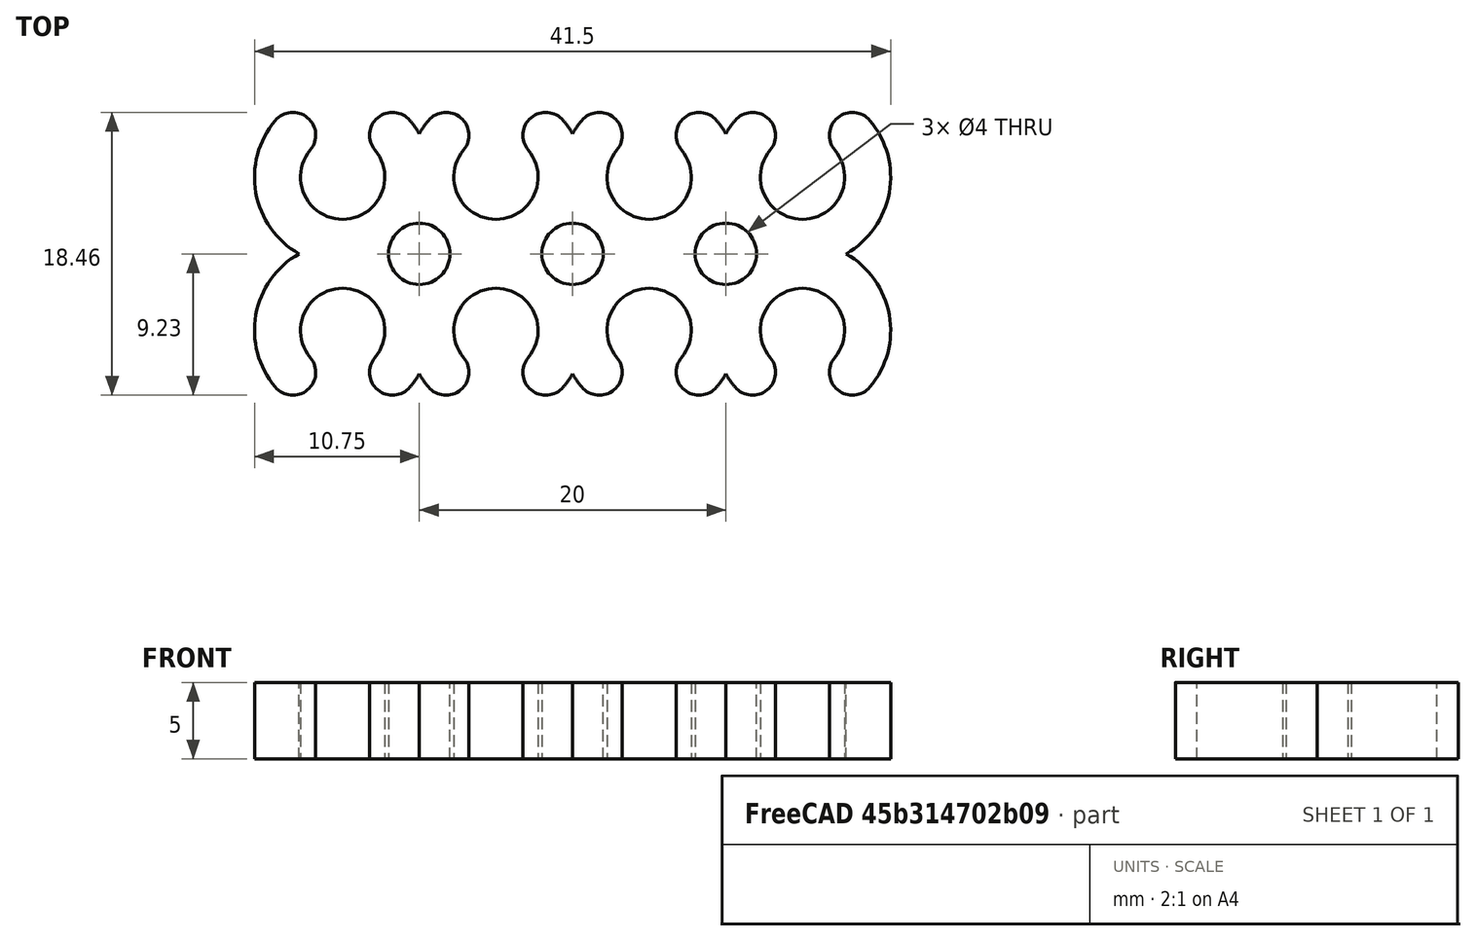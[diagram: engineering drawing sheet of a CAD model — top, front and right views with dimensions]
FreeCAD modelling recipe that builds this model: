
FCSTD DOCUMENT  (FreeCAD 0.19R24276 (Git))
Label: EthernetCableBondage
License: All rights reserved
LicenseURL: http://en.wikipedia.org/wiki/All_rights_reserved
objects: TechDraw::DrawViewDimension×4, Sketcher::SketchObject×1, PartDesign::Pad×1, PartDesign::Body×1, TechDraw::DrawSVGTemplate×1, TechDraw::DrawViewPart×1, Spreadsheet::Sheet×1, TechDraw::DrawViewAnnotation×1, TechDraw::DrawPage×1
note: 4 computed .brp shape members not serialized (recipe doc carries the construction recipe); baked Part::Feature solids carry a one-line shape summary decoded from their .brp

FEATURE [Sketcher::SketchObject] Sketch
  FullyConstrained = true
  MapMode = 5
  Support = -> [XY_Plane]
  expr: Constraints[18] = Spreadsheet.B2
  expr: Constraints[97] = Spreadsheet.B3
  expr: Constraints[194] = Spreadsheet.B3
  expr: Constraints[59] = Spreadsheet.B2
  expr: Constraints[116] = Spreadsheet.B2
  expr: Constraints[162] = Spreadsheet.B2
  expr: Constraints[106] = Spreadsheet.B2
  expr: Constraints[149] = Spreadsheet.B3
  expr: Constraints[51] = Spreadsheet.B3
  expr: Constraints[202] = Spreadsheet.B3
  expr: Constraints[52] = Spreadsheet.B3
  expr: Constraints[148] = Spreadsheet.B3
  expr: Constraints[101] = Spreadsheet.B3
  sketch-geometry (72):
    g0: LineSegment StartX=10 StartY=15 StartZ=0 EndX=40 EndY=15 EndZ=0
    g1: LineSegment StartX=10 StartY=20 StartZ=0 EndX=10 EndY=10 EndZ=0
    g2: LineSegment StartX=20 StartY=20 StartZ=0 EndX=20 EndY=10 EndZ=0
    g3: LineSegment StartX=30 StartY=20 StartZ=0 EndX=30 EndY=10 EndZ=0
    g4: LineSegment StartX=40 StartY=20 StartZ=0 EndX=40 EndY=10 EndZ=0
    g5: ArcOfCircle CenterX=10 CenterY=20 CenterZ=0 NormalX=0 NormalY=0 NormalZ=1 AngleXU=0 Radius=2.75 StartAngle=2.44346 EndAngle=6.98132
    g6: ArcOfCircle CenterX=10 CenterY=10 CenterZ=0 NormalX=0 NormalY=0 NormalZ=1 AngleXU=0 Radius=2.75 StartAngle=5.58505 EndAngle=10.1229
    g7: ArcOfCircle CenterX=10 CenterY=20 CenterZ=0 NormalX=0 NormalY=0 NormalZ=1 AngleXU=0 Radius=5.75 StartAngle=2.44346 EndAngle=4.19591
    g8: ArcOfCircle CenterX=10 CenterY=10 CenterZ=0 NormalX=0 NormalY=0 NormalZ=1 AngleXU=0 Radius=5.75 StartAngle=2.08727 EndAngle=3.83972
    g9: ArcOfCircle CenterX=10 CenterY=20 CenterZ=0 NormalX=0 NormalY=0 NormalZ=1 AngleXU=0 Radius=5.75 StartAngle=0.516475 EndAngle=0.698132
    g10: ArcOfCircle CenterX=10 CenterY=10 CenterZ=0 NormalX=0 NormalY=0 NormalZ=1 AngleXU=0 Radius=5.75 StartAngle=5.58505 EndAngle=5.76671
    g11: ArcOfCircle CenterX=6.74431 CenterY=22.7318 CenterZ=0 NormalX=0 NormalY=0 NormalZ=1 AngleXU=0 Radius=1.5 StartAngle=5.58505 EndAngle=8.72665
    g12: ArcOfCircle CenterX=13.2557 CenterY=22.7318 CenterZ=0 NormalX=0 NormalY=0 NormalZ=1 AngleXU=0 Radius=1.5 StartAngle=0.698132 EndAngle=3.83972
    g13: ArcOfCircle CenterX=6.74431 CenterY=7.26815 CenterZ=0 NormalX=0 NormalY=0 NormalZ=1 AngleXU=0 Radius=1.5 StartAngle=3.83972 EndAngle=6.98132
    g14: ArcOfCircle CenterX=13.2557 CenterY=7.26815 CenterZ=0 NormalX=0 NormalY=0 NormalZ=1 AngleXU=0 Radius=1.5 StartAngle=2.44346 EndAngle=5.58505
    g15: LineSegment StartX=10 StartY=20 StartZ=0 EndX=5.59524 EndY=23.696 EndZ=0
    g16: LineSegment StartX=10 StartY=20 StartZ=0 EndX=14.4048 EndY=23.696 EndZ=0
    g17: LineSegment StartX=10 StartY=10 StartZ=0 EndX=5.59524 EndY=6.30397 EndZ=0
    g18: LineSegment StartX=10 StartY=10 StartZ=0 EndX=14.4048 EndY=6.30397 EndZ=0
    g19: ArcOfCircle CenterX=20 CenterY=20 CenterZ=0 NormalX=0 NormalY=0 NormalZ=1 AngleXU=0 Radius=2.75 StartAngle=2.44346 EndAngle=6.98132
    g20: ArcOfCircle CenterX=20 CenterY=10 CenterZ=0 NormalX=0 NormalY=0 NormalZ=1 AngleXU=0 Radius=2.75 StartAngle=5.58505 EndAngle=10.1229
    g21: ArcOfCircle CenterX=20 CenterY=20 CenterZ=0 NormalX=0 NormalY=0 NormalZ=1 AngleXU=0 Radius=5.75 StartAngle=2.44346 EndAngle=2.62512
    g22: ArcOfCircle CenterX=16.7443 CenterY=22.7318 CenterZ=0 NormalX=0 NormalY=0 NormalZ=1 AngleXU=0 Radius=1.5 StartAngle=5.58505 EndAngle=8.72665
    g23: LineSegment StartX=20 StartY=20 StartZ=0 EndX=15.5952 EndY=23.696 EndZ=0
    g24: LineSegment StartX=7.89338 StartY=21.7677 StartZ=0 EndX=12.1066 EndY=21.7677 EndZ=0
    g25: LineSegment StartX=7.89338 StartY=8.23233 StartZ=0 EndX=12.1066 EndY=8.23233 EndZ=0
    g26: ArcOfCircle CenterX=20 CenterY=20 CenterZ=0 NormalX=0 NormalY=0 NormalZ=1 AngleXU=0 Radius=5.75 StartAngle=0.516475 EndAngle=0.698132
    g27: ArcOfCircle CenterX=20 CenterY=10 CenterZ=0 NormalX=0 NormalY=0 NormalZ=1 AngleXU=0 Radius=5.75 StartAngle=3.65807 EndAngle=3.83972
    g28: ArcOfCircle CenterX=20 CenterY=10 CenterZ=0 NormalX=0 NormalY=0 NormalZ=1 AngleXU=0 Radius=5.75 StartAngle=5.58505 EndAngle=5.76671
    g29: ArcOfCircle CenterX=16.7443 CenterY=7.26815 CenterZ=0 NormalX=0 NormalY=0 NormalZ=1 AngleXU=0 Radius=1.5 StartAngle=3.83972 EndAngle=6.98132
    g30: ArcOfCircle CenterX=23.2557 CenterY=7.26815 CenterZ=0 NormalX=0 NormalY=0 NormalZ=1 AngleXU=0 Radius=1.5 StartAngle=2.44346 EndAngle=5.58505
    g31: ArcOfCircle CenterX=23.2557 CenterY=22.7318 CenterZ=0 NormalX=0 NormalY=0 NormalZ=1 AngleXU=0 Radius=1.5 StartAngle=0.698132 EndAngle=3.83972
    g32: LineSegment StartX=20 StartY=20 StartZ=0 EndX=24.4048 EndY=23.696 EndZ=0
    g33: LineSegment StartX=20 StartY=10 StartZ=0 EndX=15.5952 EndY=6.30397 EndZ=0
    g34: LineSegment StartX=20 StartY=10 StartZ=0 EndX=24.4048 EndY=6.30397 EndZ=0
    g35: LineSegment StartX=17.8934 StartY=21.7677 StartZ=0 EndX=22.1066 EndY=21.7677 EndZ=0
    g36: LineSegment StartX=17.8934 StartY=8.23233 StartZ=0 EndX=22.1066 EndY=8.23233 EndZ=0
    g37: Circle CenterX=15 CenterY=15 CenterZ=0 NormalX=0 NormalY=0 NormalZ=1 AngleXU=0 Radius=2
    g38: ArcOfCircle CenterX=30 CenterY=20 CenterZ=0 NormalX=0 NormalY=0 NormalZ=1 AngleXU=0 Radius=2.75 StartAngle=2.44346 EndAngle=6.98132
    g39: ArcOfCircle CenterX=30 CenterY=20 CenterZ=0 NormalX=0 NormalY=0 NormalZ=1 AngleXU=0 Radius=5.75 StartAngle=2.44346 EndAngle=2.62512
    g40: ArcOfCircle CenterX=30 CenterY=20 CenterZ=0 NormalX=0 NormalY=0 NormalZ=1 AngleXU=0 Radius=5.75 StartAngle=0.516475 EndAngle=0.698132
    g41: ArcOfCircle CenterX=30 CenterY=10 CenterZ=0 NormalX=0 NormalY=0 NormalZ=1 AngleXU=0 Radius=2.75 StartAngle=5.58505 EndAngle=10.1229
    g42: ArcOfCircle CenterX=30 CenterY=10 CenterZ=0 NormalX=0 NormalY=0 NormalZ=1 AngleXU=0 Radius=5.75 StartAngle=3.65807 EndAngle=3.83972
    g43: ArcOfCircle CenterX=30 CenterY=10 CenterZ=0 NormalX=0 NormalY=0 NormalZ=1 AngleXU=0 Radius=5.75 StartAngle=5.58505 EndAngle=5.76671
    g44: ArcOfCircle CenterX=26.7443 CenterY=22.7318 CenterZ=0 NormalX=0 NormalY=0 NormalZ=1 AngleXU=0 Radius=1.5 StartAngle=5.58505 EndAngle=8.72665
    g45: ArcOfCircle CenterX=26.7443 CenterY=7.26815 CenterZ=0 NormalX=0 NormalY=0 NormalZ=1 AngleXU=0 Radius=1.5 StartAngle=3.83972 EndAngle=6.98132
    g46: ArcOfCircle CenterX=33.2557 CenterY=22.7318 CenterZ=0 NormalX=0 NormalY=0 NormalZ=1 AngleXU=0 Radius=1.5 StartAngle=0.698132 EndAngle=3.83972
    g47: ArcOfCircle CenterX=33.2557 CenterY=7.26815 CenterZ=0 NormalX=0 NormalY=0 NormalZ=1 AngleXU=0 Radius=1.5 StartAngle=2.44346 EndAngle=5.58505
    g48: LineSegment StartX=30 StartY=20 StartZ=0 EndX=25.5952 EndY=23.696 EndZ=0
    g49: LineSegment StartX=30 StartY=20 StartZ=0 EndX=34.4048 EndY=23.696 EndZ=0
    g50: LineSegment StartX=30 StartY=10 StartZ=0 EndX=25.5952 EndY=6.30397 EndZ=0
    g51: LineSegment StartX=30 StartY=10 StartZ=0 EndX=34.4048 EndY=6.30397 EndZ=0
    g52: LineSegment StartX=27.8934 StartY=21.7677 StartZ=0 EndX=32.1066 EndY=21.7677 EndZ=0
    g53: LineSegment StartX=27.8934 StartY=8.23233 StartZ=0 EndX=32.1066 EndY=8.23233 EndZ=0
    g54: ArcOfCircle CenterX=40 CenterY=20 CenterZ=0 NormalX=0 NormalY=0 NormalZ=1 AngleXU=0 Radius=2.75 StartAngle=2.44346 EndAngle=6.98132
    g55: ArcOfCircle CenterX=40 CenterY=20 CenterZ=0 NormalX=0 NormalY=0 NormalZ=1 AngleXU=0 Radius=5.75 StartAngle=2.44346 EndAngle=2.62512
    g56: ArcOfCircle CenterX=40 CenterY=20 CenterZ=0 NormalX=0 NormalY=0 NormalZ=1 AngleXU=0 Radius=5.75 StartAngle=5.22886 EndAngle=6.98132
    g57: ArcOfCircle CenterX=40 CenterY=10 CenterZ=0 NormalX=0 NormalY=0 NormalZ=1 AngleXU=0 Radius=2.75 StartAngle=5.58505 EndAngle=10.1229
    g58: ArcOfCircle CenterX=40 CenterY=10 CenterZ=0 NormalX=0 NormalY=0 NormalZ=1 AngleXU=0 Radius=5.75 StartAngle=3.65807 EndAngle=3.83972
    g59: ArcOfCircle CenterX=40 CenterY=10 CenterZ=0 NormalX=0 NormalY=0 NormalZ=1 AngleXU=0 Radius=5.75 StartAngle=5.58505 EndAngle=7.33751
    g60: ArcOfCircle CenterX=36.7443 CenterY=22.7318 CenterZ=0 NormalX=0 NormalY=0 NormalZ=1 AngleXU=0 Radius=1.5 StartAngle=5.58505 EndAngle=8.72665
    g61: ArcOfCircle CenterX=43.2557 CenterY=22.7318 CenterZ=0 NormalX=0 NormalY=0 NormalZ=1 AngleXU=0 Radius=1.5 StartAngle=0.698132 EndAngle=3.83972
    g62: ArcOfCircle CenterX=36.7443 CenterY=7.26815 CenterZ=0 NormalX=0 NormalY=0 NormalZ=1 AngleXU=0 Radius=1.5 StartAngle=3.83972 EndAngle=6.98132
    g63: ArcOfCircle CenterX=43.2557 CenterY=7.26815 CenterZ=0 NormalX=0 NormalY=0 NormalZ=1 AngleXU=0 Radius=1.5 StartAngle=2.44346 EndAngle=5.58505
    g64: LineSegment StartX=40 StartY=20 StartZ=0 EndX=35.5952 EndY=23.696 EndZ=0
    g65: LineSegment StartX=40 StartY=20 StartZ=0 EndX=44.4048 EndY=23.696 EndZ=0
    g66: LineSegment StartX=40 StartY=10 StartZ=0 EndX=35.5952 EndY=6.30397 EndZ=0
    g67: LineSegment StartX=40 StartY=10 StartZ=0 EndX=44.4048 EndY=6.30397 EndZ=0
    g68: LineSegment StartX=37.8934 StartY=21.7677 StartZ=0 EndX=42.1066 EndY=21.7677 EndZ=0
    g69: LineSegment StartX=37.8934 StartY=8.23233 StartZ=0 EndX=42.1066 EndY=8.23233 EndZ=0
    g70: Circle CenterX=25 CenterY=15 CenterZ=0 NormalX=0 NormalY=0 NormalZ=1 AngleXU=0 Radius=2
    g71: Circle CenterX=35 CenterY=15 CenterZ=0 NormalX=0 NormalY=0 NormalZ=1 AngleXU=0 Radius=2
  constraints (209):
    c: Horizontal(g0)
    c: DistanceX(g-1,g0) = 10
    c: DistanceY(g-1,g0) = 15
    c: DistanceX(g0,g0) = 30
    c: PointOnObject(g0,g1)
    c: Symmetric(g1,g1,g0)
    c: DistanceY(g1,g1) = 10
    c: DistanceY(g2,g2) = 10
    c: Symmetric(g2,g2,g0)
    c: DistanceX(g1,g2) = 10
    c: Symmetric(g3,g3,g0)
    c: DistanceY(g3,g3) = 10
    c: DistanceX(g2,g3) = 10
    c: PointOnObject(g0,g4)
    c: DistanceY(g4,g4) = 10
    c: Symmetric(g4,g4,g0)
    c: Coincident(g5,g1)
    c: Coincident(g6,g1)
    c: Radius(g5) = 2.75
    c: Equal(g5,g6)
    c: Coincident(g7,g5)
    c: Coincident(g8,g6)
    c: Coincident(g7,g8)
    c: Radius(g7) = 5.75
    c: Equal(g7,g8)
    c: Coincident(g9,g5)
    c: Coincident(g10,g6)
    c: Coincident(g11,g7)
    c: Coincident(g11,g5)
    c: Coincident(g12,g5)
    c: Coincident(g12,g9)
    c: Coincident(g13,g8)
    c: Coincident(g13,g6)
    c: Coincident(g14,g6)
    c: Coincident(g14,g10)
    c: Coincident(g15,g5)
    c: Coincident(g15,g7)
    c: Coincident(g16,g5)
    c: Coincident(g16,g9)
    c: Coincident(g17,g6)
    c: Coincident(g17,g8)
    c: Coincident(g18,g6)
    c: Coincident(g18,g10)
    c: PointOnObject(g5,g15)
    c: PointOnObject(g11,g15)
    c: PointOnObject(g5,g16)
    c: PointOnObject(g12,g16)
    c: PointOnObject(g6,g17)
    c: PointOnObject(g13,g17)
    c: PointOnObject(g6,g18)
    c: PointOnObject(g14,g18)
    c: Angle(g16,g15) = 1.74533
    c: Angle(g17,g18) = 1.74533
    c: Coincident(g19,g2)
    c: Coincident(g20,g2)
    c: Radius(g9) = 5.75
    c: Coincident(g21,g19)
    c: Radius(g21) = 5.75
    c: Coincident(g21,g9)
    c: Radius(g19) = 2.75
    c: Coincident(g22,g21)
    c: Coincident(g22,g19)
    c: Coincident(g23,g19)
    c: Coincident(g23,g21)
    c: PointOnObject(g19,g23)
    c: PointOnObject(g22,g23)
    c: Coincident(g24,g5)
    c: Coincident(g24,g5)
    c: Horizontal(g24)
    c: Coincident(g25,g6)
    c: Coincident(g25,g6)
    c: Horizontal(g25)
    c: Coincident(g26,g19)
    c: Coincident(g27,g20)
    c: Radius(g10) = 5.75
    c: Coincident(g10,g27)
    c: Coincident(g28,g20)
    c: Coincident(g29,g27)
    c: Coincident(g29,g20)
    c: Coincident(g30,g20)
    c: Coincident(g30,g28)
    c: Coincident(g31,g19)
    c: Coincident(g31,g26)
    c: Radius(g26) = 5.75
    c: Radius(g28) = 5.75
    c: Coincident(g32,g19)
    c: Coincident(g32,g26)
    c: Coincident(g33,g20)
    c: Coincident(g33,g27)
    c: Coincident(g34,g20)
    c: Coincident(g34,g28)
    c: PointOnObject(g20,g33)
    c: PointOnObject(g29,g33)
    c: PointOnObject(g30,g34)
    c: PointOnObject(g20,g34)
    c: PointOnObject(g19,g32)
    c: PointOnObject(g31,g32)
    c: Angle(g32,g23) = 1.74533
    c: Coincident(g35,g19)
    c: Coincident(g35,g19)
    c: Horizontal(g35)
    c: Angle(g33,g34) = 1.74533
    c: Coincident(g36,g20)
    c: Coincident(g36,g20)
    c: Horizontal(g36)
    c: Radius(g27) = 5.75
    c: Radius(g20) = 2.75
    c: PointOnObject(g37,g0)
    c: Radius(g37) = 2
    c: DistanceX(g0,g37) = 5
    c: Coincident(g38,g3)
    c: Coincident(g39,g38)
    c: Coincident(g40,g38)
    c: Coincident(g41,g3)
    c: Coincident(g42,g41)
    c: Coincident(g43,g41)
    c: Radius(g38) = 2.75
    c: Equal(g38,g41)
    c: Radius(g39) = 5.75
    c: Equal(g39,g40)
    c: Equal(g39,g43)
    c: Equal(g39,g42)
    c: Coincident(g26,g39)
    c: Coincident(g28,g42)
    c: Coincident(g44,g39)
    c: Coincident(g44,g38)
    c: Coincident(g45,g41)
    c: Coincident(g45,g42)
    c: Coincident(g46,g38)
    c: Coincident(g46,g40)
    c: Coincident(g47,g41)
    c: Coincident(g47,g43)
    c: Coincident(g48,g38)
    c: Coincident(g48,g39)
    c: Coincident(g49,g38)
    c: Coincident(g49,g40)
    c: Coincident(g50,g41)
    c: Coincident(g50,g42)
    c: Coincident(g51,g41)
    c: Coincident(g51,g43)
    c: PointOnObject(g44,g48)
    c: PointOnObject(g38,g48)
    c: PointOnObject(g46,g49)
    c: PointOnObject(g38,g49)
    c: PointOnObject(g45,g50)
    c: PointOnObject(g41,g50)
    c: PointOnObject(g47,g51)
    c: PointOnObject(g41,g51)
    c: Angle(g49,g48) = 1.74533
    c: Angle(g50,g51) = 1.74533
    c: Coincident(g52,g38)
    c: Coincident(g52,g38)
    c: Coincident(g53,g41)
    c: Coincident(g53,g41)
    c: Horizontal(g52)
    c: Horizontal(g53)
    c: Coincident(g54,g4)
    c: Coincident(g55,g54)
    c: Coincident(g56,g54)
    c: Coincident(g57,g4)
    c: Coincident(g58,g57)
    c: Coincident(g59,g57)
    c: Radius(g54) = 2.75
    c: Equal(g54,g57)
    c: Radius(g55) = 5.75
    c: Equal(g55,g56)
    c: Equal(g55,g59)
    c: Equal(g55,g58)
    c: Coincident(g43,g58)
    c: Coincident(g40,g55)
    c: Coincident(g59,g56)
    c: Coincident(g60,g55)
    c: Coincident(g60,g54)
    c: Coincident(g61,g54)
    c: Coincident(g61,g56)
    c: Coincident(g62,g58)
    c: Coincident(g62,g57)
    c: Coincident(g63,g57)
    c: Coincident(g63,g59)
    c: Coincident(g64,g54)
    c: Coincident(g64,g55)
    c: Coincident(g65,g54)
    c: Coincident(g65,g56)
    c: Coincident(g66,g57)
    c: Coincident(g66,g58)
    c: Coincident(g67,g57)
    c: Coincident(g67,g59)
    c: PointOnObject(g60,g64)
    c: PointOnObject(g54,g64)
    c: PointOnObject(g61,g65)
    c: PointOnObject(g54,g65)
    c: Coincident(g68,g54)
    c: Coincident(g68,g54)
    c: Horizontal(g68)
    c: Angle(g65,g64) = 1.74533
    c: PointOnObject(g62,g66)
    c: PointOnObject(g57,g66)
    c: PointOnObject(g63,g67)
    c: PointOnObject(g57,g67)
    c: Coincident(g69,g57)
    c: Coincident(g69,g57)
    c: Horizontal(g69)
    c: Angle(g66,g67) = 1.74533
    c: PointOnObject(g70,g0)
    c: PointOnObject(g71,g0)
    c: Radius(g70) = 2
    c: Radius(g71) = 2
    c: DistanceX(g71,g0) = 5
    c: DistanceX(g70,g71) = 10
FEATURE [PartDesign::Pad] Pad
  Direction = (1,1,1)
  Length = 5
  Length2 = 100
  Profile = -> Sketch
  Type = 0
FEATURE [PartDesign::Body] Body
  Group = -> [Sketch,Pad]
  Origin = -> Origin
  Tip = -> Pad
FEATURE [TechDraw::DrawSVGTemplate] Template
  EditableTexts = Designed_by_Name=Khramushin Igor; Drawing_number=1; FC-Date=01.06.2021; FC-SC=3:1; FC-SH=1; FC-Title=Ethernet Cable Bondage; Subtitle=ABS plastic; Weight=0,0024
  Height = 210
  Orientation = 1
  Width = 297
FEATURE [TechDraw::DrawViewPart] View
  CoarseView = false
  Direction = (0,0,1)
  Focus = 100
  HardHidden = false
  IsoCount = 0
  IsoHidden = false
  IsoVisible = false
  LockPosition = false
  Perspective = false
  Rotation = 0
  Scale = 3
  ScaleType = 0
  SeamHidden = false
  SeamVisible = true
  SmoothHidden = false
  SmoothVisible = true
  Source = -> [Body]
  X = 134.272
  XDirection = (1,0,0)
  Y = 122.927
FEATURE [TechDraw::DrawViewDimension] Dimension
  Arbitrary = false
  ArbitraryTolerances = false
  EqualTolerance = true
  FormatSpec = R%.2f
  FormatSpecOverTolerance = %+.2f
  FormatSpecUnderTolerance = %+.2f
  Inverted = false
  LockPosition = false
  MeasureType = 1
  OverTolerance = 0
  References2D = -> [View]
  Rotation = 0
  Scale = 3
  ScaleType = 0
  TheoreticalExact = false
  Type = 4
  UnderTolerance = 0
  X = -80.2439
  Y = 21.626
FEATURE [TechDraw::DrawViewDimension] Dimension001
  Arbitrary = false
  ArbitraryTolerances = false
  EqualTolerance = true
  FormatSpec = R%.2f
  FormatSpecOverTolerance = %+.2f
  FormatSpecUnderTolerance = %+.2f
  Inverted = false
  LockPosition = false
  MeasureType = 1
  OverTolerance = 0
  References2D = -> [View]
  Rotation = 0
  Scale = 3
  ScaleType = 0
  TheoreticalExact = false
  Type = 4
  UnderTolerance = 0
  X = 81.6667
  Y = 20.4878
FEATURE [TechDraw::DrawViewDimension] Dimension002
  Arbitrary = false
  ArbitraryTolerances = false
  EqualTolerance = true
  FormatSpec = %.2f
  FormatSpecOverTolerance = %+.2f
  FormatSpecUnderTolerance = %+.2f
  Inverted = false
  LockPosition = false
  MeasureType = 1
  OverTolerance = 0
  References2D = -> [View]
  Rotation = 0
  Scale = 3
  ScaleType = 0
  TheoreticalExact = false
  Type = 6
  UnderTolerance = 0
  X = -45.3821
  Y = -49.7967
FEATURE [TechDraw::DrawViewDimension] Dimension003
  Arbitrary = false
  ArbitraryTolerances = false
  EqualTolerance = true
  FormatSpec = ⌀%.2f
  FormatSpecOverTolerance = %+.2f
  FormatSpecUnderTolerance = %+.2f
  Inverted = false
  LockPosition = false
  MeasureType = 1
  OverTolerance = 0
  References2D = -> [View]
  Rotation = 0
  Scale = 3
  ScaleType = 0
  TheoreticalExact = false
  Type = 5
  UnderTolerance = 0
  X = -79.3902
  Y = -2.84553
FEATURE [Spreadsheet::Sheet] Spreadsheet
  cells = A2=Inner radius (mm); B2=2.75; A3=Angle ; B3=100
FEATURE [TechDraw::DrawViewAnnotation] Annotation
  Font = osifont
  LineSpace = 80
  LockPosition = false
  MaxWidth = -1
  Rotation = 0
  Scale = 3
  ScaleType = 0
  Text = Volume = 2235.373221922522
  TextSize = 5
  TextStyle = 0
  X = 84.1643
  Y = 39.3691
FEATURE [TechDraw::DrawPage] Page
  KeepUpdated = true
  NextBalloonIndex = 1
  ProjectionType = 0
  Scale = 3
  Template = -> Template
  Views = -> [View,Dimension,Dimension001,Dimension002,Dimension003,Annotation]
